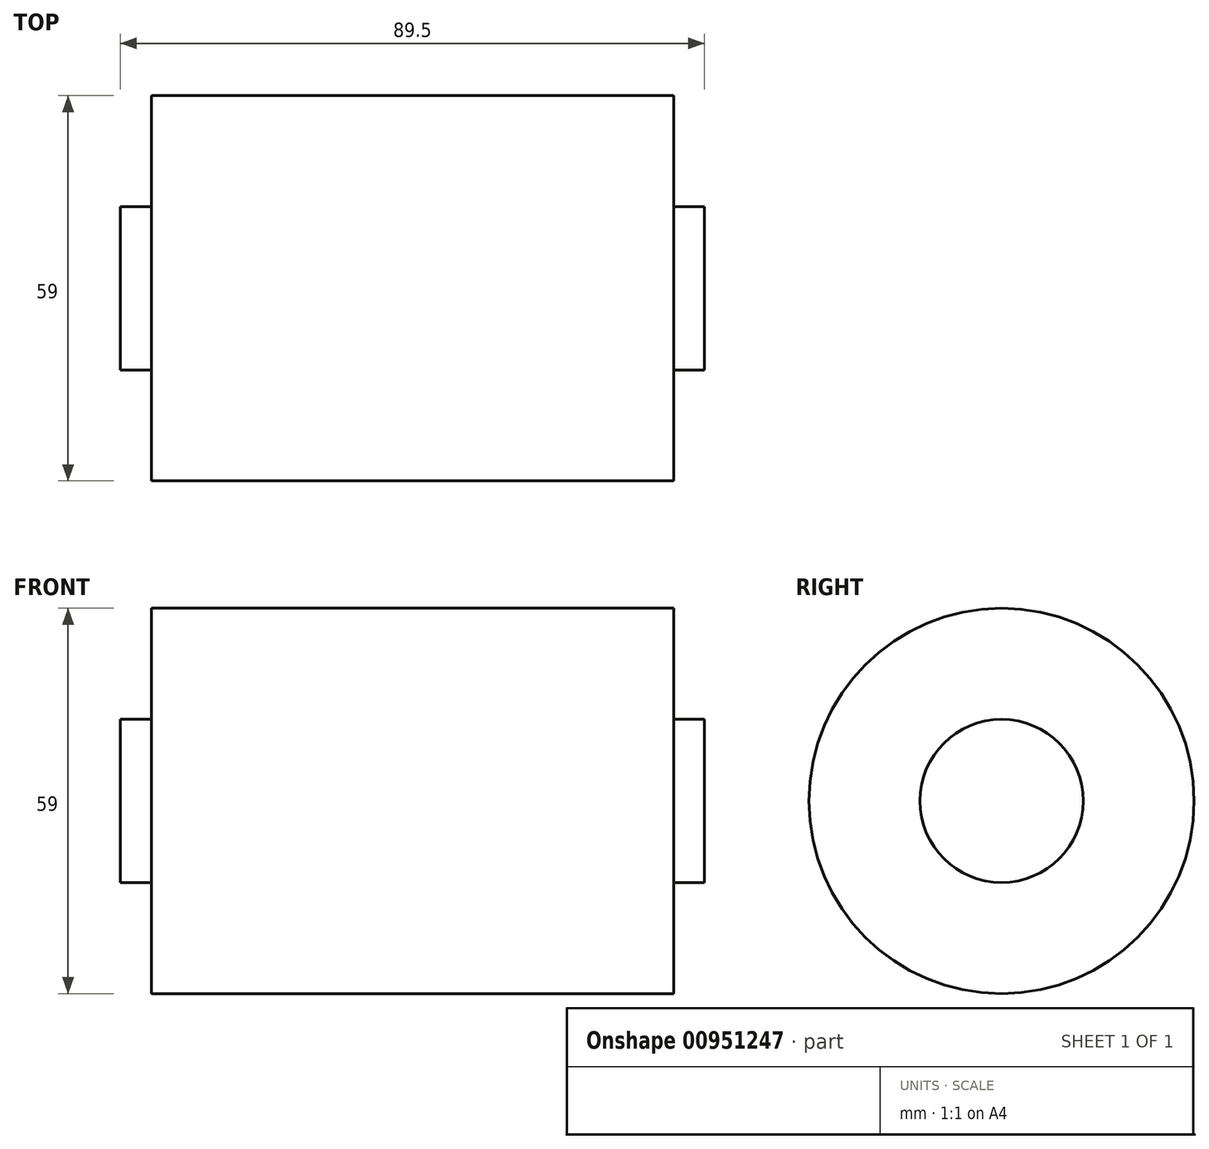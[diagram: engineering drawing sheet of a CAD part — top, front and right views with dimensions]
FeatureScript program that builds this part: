
annotation { "Feature Type Name" : "Feature", "Feature Type Description" : "" }
export const myFeature = defineFeature(function(context is Context, id is Id, definition is map)
    precondition{}
    {
        {
            var Q0;
            Q0=qCreatedBy(makeId("Right.planeOp"),FACE);
            var sketch = newSketch(context, id + "F0", { "sketchPlane" : qUnion([Q0])});
            skCircle(sketch, "E0", {"center": v(0, 0) * mm, "radius": 29.5 * mm});
            skCircle(sketch, "E1", {"center": v(0, 0) * mm, "radius": 12.5 * mm});
            skSolve(sketch);
        }
        {
            var Q0;
            Q0=makeQuery(id+"F0.imprint","IMPRINT",FACE,{"disambiguationData":[TD([[makeQuery(id+"F0.imprint","IMPRINT",EDGE,{"derivedFrom":sQuery(id+"F0.wireOp",EDGE,"E0")}),1.0]])]});
            extrude(context, id + "F1", {"entities" : qUnion([Q0]), "endBound" : BoundingType.SYMMETRIC, "depth" : 80 * mm, "offsetDistance" : 25 * mm});
        }
        {
            var Q0;
            Q0=makeQuery(id+"F0.imprint","IMPRINT",FACE,{"disambiguationData":[TD([[makeQuery(id+"F0.imprint","IMPRINT",EDGE,{"derivedFrom":sQuery(id+"F0.wireOp",EDGE,"E1")}),1.0]])]});
            extrude(context, id + "F2", {"entities" : qUnion([Q0]), "operationType" : NewBodyOperationType.ADD, "endBound" : BoundingType.SYMMETRIC, "depth" : 89.5 * mm, "offsetDistance" : 25 * mm});
        }
    });
